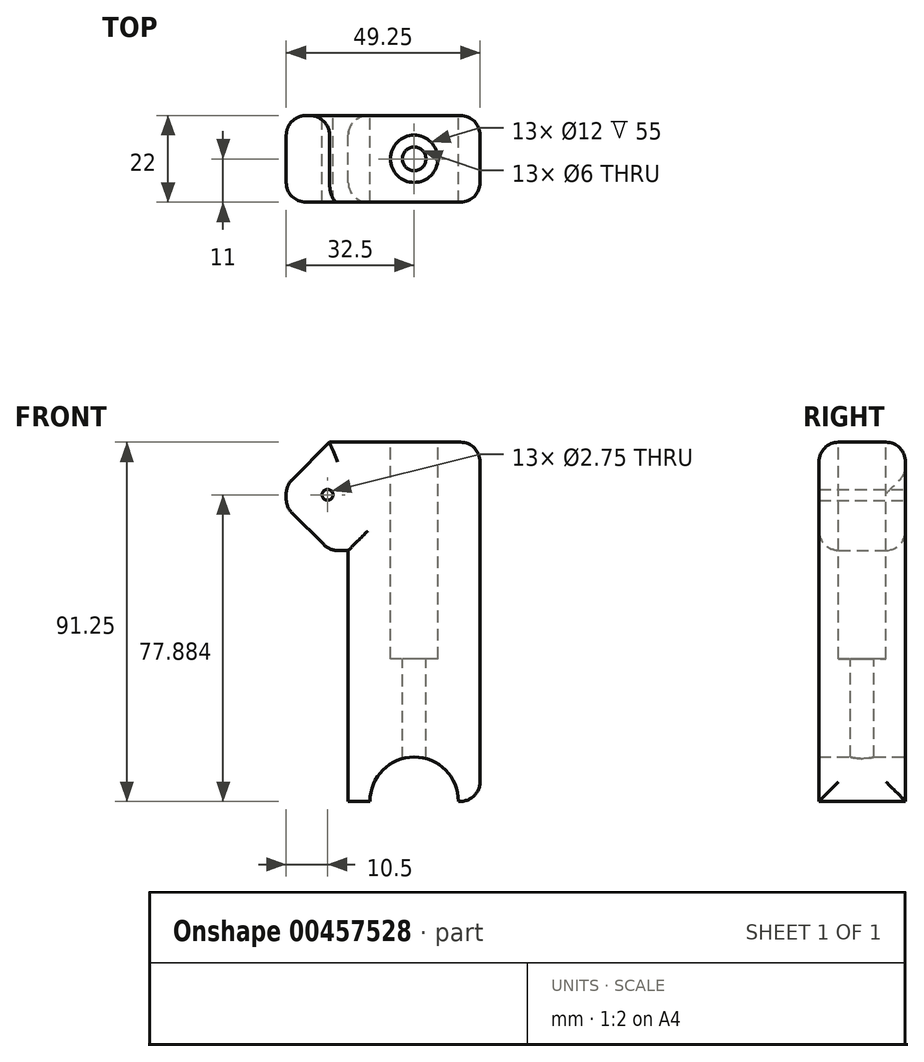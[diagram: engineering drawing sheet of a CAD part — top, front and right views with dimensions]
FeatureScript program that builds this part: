
annotation { "Feature Type Name" : "Feature", "Feature Type Description" : "" }
export const myFeature = defineFeature(function(context is Context, id is Id, definition is map)
    precondition{}
    {
        {
            var Q0;
            Q0=qCreatedBy(makeId("Front.planeOp"),FACE);
            var sketch = newSketch(context, id + "F0", { "sketchPlane" : qUnion([Q0])});
            skCircle(sketch, "E0", {"center": v(0, 0) * mm, "radius": 11.25 * mm});
            skCircle(sketch, "E1", {"center": v(0, 0) * mm, "radius": 16.75 * mm});
            skLineSegment(sketch, "E2", {"start": v(0, 11.25) * mm, "end": v(0, 36.25) * mm, "construction": true});
            skLineSegment(sketch, "E3.bottom", {"start": v(27.5, 36.25) * mm, "end": v(-27.5, 36.25) * mm});
            skLineSegment(sketch, "E3.top", {"start": v(27.5, -36.25) * mm, "end": v(-27.5, -36.25) * mm});
            skLineSegment(sketch, "E3.left", {"start": v(27.5, 36.25) * mm, "end": v(27.5, -36.25) * mm});
            skLineSegment(sketch, "E3.right", {"start": v(-27.5, 36.25) * mm, "end": v(-27.5, -36.25) * mm});
            skLineSegment(sketch, "E4", {"start": v(0, 36.25) * mm, "end": v(0, 91.25) * mm, "construction": true});
            skLineSegment(sketch, "E5.top", {"start": v(27.5, 91.25) * mm, "end": v(-27.5, 91.25) * mm});
            skLineSegment(sketch, "E5.left", {"start": v(27.5, 36.25) * mm, "end": v(27.5, 91.25) * mm});
            skLineSegment(sketch, "E5.right", {"start": v(-27.5, 36.25) * mm, "end": v(-27.5, 91.25) * mm});
            skPoint(sketch, "E5.middle", {"position": v(0, 63.75) * mm});
            skLineSegment(sketch, "E6", {"start": v(-27.5, 0) * mm, "end": v(27.5, 0) * mm});
            skLineSegment(sketch, "E7.bottom", {"start": v(-16.75, 63.75) * mm, "end": v(16.75, 63.75) * mm});
            skLineSegment(sketch, "E7.top", {"start": v(-16.75, -63.75) * mm, "end": v(16.75, -63.75) * mm});
            skLineSegment(sketch, "E7.left", {"start": v(-16.75, 63.75) * mm, "end": v(-16.75, -63.75) * mm});
            skLineSegment(sketch, "E7.right", {"start": v(16.75, 63.75) * mm, "end": v(16.75, -63.75) * mm});
            skLineSegment(sketch, "E8", {"start": v(-16.75, 63.75) * mm, "end": v(-27.5, 63.75) * mm});
            skLineSegment(sketch, "E9", {"start": v(16.75, 63.75) * mm, "end": v(27.5, 63.75) * mm});
            skLineSegment(sketch, "E10", {"start": v(16.75, 63.75) * mm, "end": v(16.75, 91.25) * mm});
            skLineSegment(sketch, "E11", {"start": v(0, 77.88) * mm, "end": v(-22, 77.88) * mm, "construction": true});
            skCircle(sketch, "E12", {"center": v(-22, 77.88) * mm, "radius": 1.38 * mm});
            skLineSegment(sketch, "E13", {"start": v(-27.5, 91.25) * mm, "end": v(-32.5, 91.25) * mm});
            skLineSegment(sketch, "E14", {"start": v(-32.5, 91.25) * mm, "end": v(-32.5, 63.78) * mm});
            skLineSegment(sketch, "E15", {"start": v(-32.5, 63.78) * mm, "end": v(-27.5, 63.75) * mm});
            skLineSegment(sketch, "E16", {"start": v(0, 70.14) * mm, "end": v(-5.5, 70.14) * mm, "construction": true});
            skLineSegment(sketch, "E17", {"start": v(-5.5, 63.75) * mm, "end": v(-5.5, 91.25) * mm});
            skSolve(sketch);
        }
        {
            var Q0;
            {var subQ5=sQuery(id+"F0.wireOp",EDGE,"E7.bottom");Q0=makeQuery(id+"F0.imprint","IMPRINT",FACE,{"disambiguationData":[TD([[makeQuery(id+"F0.imprint","IMPRINT",EDGE,{"derivedFrom":subQ5}),-1.0]])]});}
            var Q1;
            {var subQ4=sQuery(id+"F0.wireOp",EDGE,"E7.right");var subQ6=sQuery(id+"F0.wireOp",EDGE,"E3.bottom");var subQ7=makeQuery(id+"F0.imprint","INTERSECT",VERTEX,{"derivedFrom":[subQ6,subQ4]});Q1=makeQuery(id+"F0.imprint","IMPRINT",FACE,{"disambiguationData":[TD([[makeQuery(id+"F0.imprint","IMPRINT",EDGE,{"disambiguationData":[TD([[subQ7,-1.0]])],"derivedFrom":subQ6}),1.0]])]});}
            var Q2;
            {var subQ0=sQuery(id+"F0.wireOp",EDGE,"E6");var subQ1=sQuery(id+"F0.wireOp",EDGE,"E0");var subQ2=makeQuery(id+"F0.imprint","INTERSECT",VERTEX,{"disambiguationData":[OD(0.0)],"derivedFrom":[subQ1,subQ0]});Q2=makeQuery(id+"F0.imprint","IMPRINT",FACE,{"disambiguationData":[TD([[makeQuery(id+"F0.imprint","IMPRINT",EDGE,{"disambiguationData":[TD([[subQ2,1.0]])],"derivedFrom":subQ1}),-1.0]])]});}
            var Q3;
            Q3=makeQuery(id+"F0.imprint","IMPRINT",FACE,{"disambiguationData":[TD([[makeQuery(id+"F0.imprint","IMPRINT",EDGE,{"derivedFrom":sQuery(id+"F0.wireOp",EDGE,"E7.bottom")}),1.0]])]});
            var Q4;
            {var subQ0=sQuery(id+"F0.wireOp",EDGE,"E13");Q4=makeQuery(id+"F0.imprint","IMPRINT",FACE,{"disambiguationData":[TD([[makeQuery(id+"F0.imprint","IMPRINT",EDGE,{"derivedFrom":subQ0}),1.0]])]});}
            var Q5;
            {var subQ3=sQuery(id+"F0.wireOp",EDGE,"E8");Q5=makeQuery(id+"F0.imprint","IMPRINT",FACE,{"disambiguationData":[TD([[makeQuery(id+"F0.imprint","IMPRINT",EDGE,{"derivedFrom":subQ3}),-1.0]])]});}
            extrude(context, id + "F1", {"entities" : qUnion([Q0, Q1, Q2, Q3, Q4, Q5]), "endBound" : BoundingType.SYMMETRIC, "depth" : 22 * mm});
        }
        {
            var Q0;
            Q0=makeQuery(id+"F1.opExtrude","SWEPT_FACE",FACE,{"disambiguationData":[OSD([sQuery(id+"F0.wireOp",EDGE,"E5.top")])]});
            cPlane(context, id + "F2", {"entities" : qUnion([Q0]), "cplaneType" : CPlaneType.OFFSET, "offset" : 0 * mm, "width" : 150 * mm, "height" : 150 * mm});
        }
        {
            var Q0;
            Q0=qCreatedBy(id+"F2.planeOp",FACE);
            var sketch = newSketch(context, id + "F3", { "sketchPlane" : qUnion([Q0])});
            skCircle(sketch, "E18", {"center": v(0, 0) * mm, "radius": 6 * mm});
            skCircle(sketch, "E19", {"center": v(0, 0) * mm, "radius": 3 * mm});
            skSolve(sketch);
        }
        {
            var Q0;
            Q0=makeQuery(id+"F3.imprint","IMPRINT",FACE,{"disambiguationData":[TD([[makeQuery(id+"F3.imprint","IMPRINT",EDGE,{"derivedFrom":sQuery(id+"F3.wireOp",EDGE,"E18")}),1.0]])]});
            extrude(context, id + "F4", {"entities" : qUnion([Q0]), "operationType" : NewBodyOperationType.REMOVE, "oppositeDirection" : true, "depth" : 55 * mm});
        }
        {
            var Q0;
            Q0=makeQuery(id+"F3.imprint","IMPRINT",FACE,{"disambiguationData":[TD([[makeQuery(id+"F3.imprint","IMPRINT",EDGE,{"derivedFrom":sQuery(id+"F3.wireOp",EDGE,"E19")}),1.0]])]});
            extrude(context, id + "F5", {"entities" : qUnion([Q0]), "operationType" : NewBodyOperationType.REMOVE, "endBound" : BoundingType.THROUGH_ALL, "oppositeDirection" : true, "depth" : 25 * mm});
        }
        {
            var Q0;
            Q0=makeQuery(id+"F1.opExtrude","SWEPT_EDGE",EDGE,{"disambiguationData":[OSD([sQuery(id+"F0.wireOp",EDGE,"E14"),sQuery(id+"F0.wireOp",EDGE,"E15")])]});
            var Q1;
            Q1=makeQuery(id+"F1.opExtrude","SWEPT_EDGE",EDGE,{"disambiguationData":[OSD([sQuery(id+"F0.wireOp",EDGE,"E13"),sQuery(id+"F0.wireOp",EDGE,"E14")])]});
            chamfer(context, id + "F6", {"entities" : qUnion([Q0, Q1]), "width" : 11 * mm, "tangentPropagation" : true});
        }
        {
            var Q0;
            Q0=makeQuery(id+"F1.opExtrude","SWEPT_FACE",FACE,{"disambiguationData":[OSD([sQuery(id+"F0.wireOp",EDGE,"E7.right"),sQuery(id+"F0.wireOp",EDGE,"E10")])]});
            var Q1;
            Q1=makeQuery(id+"F1.opExtrude","CAP_EDGE",EDGE,{"disambiguationData":[OSD([sQuery(id+"F0.wireOp",EDGE,"E7.left")])],"isStart":false});
            var Q2;
            Q2=makeQuery(id+"F1.opExtrude","CAP_EDGE",EDGE,{"disambiguationData":[OSD([sQuery(id+"F0.wireOp",EDGE,"E7.left")])],"isStart":true});
            var Q3;
            {var subQ0=sQuery(id+"F0.wireOp",EDGE,"E5.right");Q3=makeQuery(id+"F6.opChamfer","BLEND_EDGE",EDGE,{"blendedFrom":[makeQuery(id+"F1.opExtrude","SWEPT_EDGE",EDGE,{"disambiguationData":[OSD([subQ0,sQuery(id+"F0.wireOp",EDGE,"E8")])]}),makeQuery(id+"F1.opExtrude","SWEPT_FACE",FACE,{"disambiguationData":[OSD([subQ0])]})],"blendedInto":[makeQuery(id+"F1.opExtrude","SWEPT_FACE",FACE,{"disambiguationData":[OSD([subQ0])]})]});}
            var Q4;
            {var subQ0=sQuery(id+"F0.wireOp",EDGE,"E5.right");Q4=makeQuery(id+"F6.opChamfer","BLEND_EDGE",EDGE,{"blendedFrom":[makeQuery(id+"F1.opExtrude","SWEPT_EDGE",EDGE,{"disambiguationData":[OSD([sQuery(id+"F0.wireOp",EDGE,"E5.top"),subQ0])]}),makeQuery(id+"F1.opExtrude","SWEPT_FACE",FACE,{"disambiguationData":[OSD([subQ0])]})],"blendedInto":[makeQuery(id+"F1.opExtrude","SWEPT_FACE",FACE,{"disambiguationData":[OSD([subQ0])]})]});}
            var Q5;
            {var subQ2=sQuery(id+"F0.wireOp",EDGE,"E5.right");var subQ7=sQuery(id+"F0.wireOp",EDGE,"E5.top");Q5=makeQuery(id+"F6.opChamfer","BLEND_EDGE",EDGE,{"blendedFrom":[makeQuery(id+"F1.opExtrude","SWEPT_EDGE",EDGE,{"disambiguationData":[OSD([subQ7,subQ2])]}),makeQuery(id+"F4.boolean.opBoolean","SPLIT",FACE,{"disambiguationData":[TD([makeQuery(id+"F1.opExtrude","SWEPT_FACE",FACE,{"disambiguationData":[OSD([subQ2])]})])],"derivedFrom":makeQuery(id+"F1.opExtrude","SWEPT_FACE",FACE,{"disambiguationData":[OSD([subQ7])]})})],"blendedInto":[makeQuery(id+"F4.boolean.opBoolean","SPLIT",FACE,{"disambiguationData":[TD([makeQuery(id+"F1.opExtrude","SWEPT_FACE",FACE,{"disambiguationData":[OSD([subQ2])]})])],"derivedFrom":makeQuery(id+"F1.opExtrude","SWEPT_FACE",FACE,{"disambiguationData":[OSD([subQ7])]})})]});}
            var Q6;
            Q6=makeQuery(id+"F1.opExtrude","CAP_EDGE",EDGE,{"disambiguationData":[OSD([sQuery(id+"F0.wireOp",EDGE,"E5.top")])],"isStart":false});
            var Q7;
            {var subQ0=sQuery(id+"F0.wireOp",EDGE,"E5.right");var subQ1=sQuery(id+"F0.wireOp",EDGE,"E5.top");Q7=makeQuery(id+"F6.opChamfer","BLEND_EDGE",EDGE,{"blendedFrom":[makeQuery(id+"F1.opExtrude","SWEPT_EDGE",EDGE,{"disambiguationData":[OSD([subQ1,subQ0])]}),makeQuery(id+"F1.opExtrude","CAP_FACE",FACE,{"disambiguationData":[OSD([sQuery(id+"F0.wireOp",EDGE,"E0"),subQ1,subQ0,sQuery(id+"F0.wireOp",EDGE,"E6"),sQuery(id+"F0.wireOp",EDGE,"E7.left"),sQuery(id+"F0.wireOp",EDGE,"E7.right"),sQuery(id+"F0.wireOp",EDGE,"E8"),sQuery(id+"F0.wireOp",EDGE,"E10"),sQuery(id+"F0.wireOp",EDGE,"E12")])],"isStart":false})],"blendedInto":[makeQuery(id+"F1.opExtrude","CAP_FACE",FACE,{"disambiguationData":[OSD([sQuery(id+"F0.wireOp",EDGE,"E0"),subQ1,subQ0,sQuery(id+"F0.wireOp",EDGE,"E6"),sQuery(id+"F0.wireOp",EDGE,"E7.left"),sQuery(id+"F0.wireOp",EDGE,"E7.right"),sQuery(id+"F0.wireOp",EDGE,"E8"),sQuery(id+"F0.wireOp",EDGE,"E10"),sQuery(id+"F0.wireOp",EDGE,"E12")])],"isStart":false})]});}
            var Q8;
            {var subQ0=sQuery(id+"F0.wireOp",EDGE,"E8");var subQ1=sQuery(id+"F0.wireOp",EDGE,"E5.right");Q8=makeQuery(id+"F6.opChamfer","BLEND_EDGE",EDGE,{"blendedFrom":[makeQuery(id+"F1.opExtrude","SWEPT_EDGE",EDGE,{"disambiguationData":[OSD([subQ1,subQ0])]}),makeQuery(id+"F1.opExtrude","CAP_FACE",FACE,{"disambiguationData":[OSD([sQuery(id+"F0.wireOp",EDGE,"E0"),sQuery(id+"F0.wireOp",EDGE,"E5.top"),subQ1,sQuery(id+"F0.wireOp",EDGE,"E6"),sQuery(id+"F0.wireOp",EDGE,"E7.left"),sQuery(id+"F0.wireOp",EDGE,"E7.right"),subQ0,sQuery(id+"F0.wireOp",EDGE,"E10"),sQuery(id+"F0.wireOp",EDGE,"E12")])],"isStart":false})],"blendedInto":[makeQuery(id+"F1.opExtrude","CAP_FACE",FACE,{"disambiguationData":[OSD([sQuery(id+"F0.wireOp",EDGE,"E0"),sQuery(id+"F0.wireOp",EDGE,"E5.top"),subQ1,sQuery(id+"F0.wireOp",EDGE,"E6"),sQuery(id+"F0.wireOp",EDGE,"E7.left"),sQuery(id+"F0.wireOp",EDGE,"E7.right"),subQ0,sQuery(id+"F0.wireOp",EDGE,"E10"),sQuery(id+"F0.wireOp",EDGE,"E12")])],"isStart":false})]});}
            var Q9;
            {var subQ0=sQuery(id+"F0.wireOp",EDGE,"E8");var subQ1=sQuery(id+"F0.wireOp",EDGE,"E5.right");Q9=makeQuery(id+"F6.opChamfer","BLEND_EDGE",EDGE,{"blendedFrom":[makeQuery(id+"F1.opExtrude","SWEPT_EDGE",EDGE,{"disambiguationData":[OSD([subQ1,subQ0])]}),makeQuery(id+"F1.opExtrude","CAP_FACE",FACE,{"disambiguationData":[OSD([sQuery(id+"F0.wireOp",EDGE,"E0"),sQuery(id+"F0.wireOp",EDGE,"E5.top"),subQ1,sQuery(id+"F0.wireOp",EDGE,"E6"),sQuery(id+"F0.wireOp",EDGE,"E7.left"),sQuery(id+"F0.wireOp",EDGE,"E7.right"),subQ0,sQuery(id+"F0.wireOp",EDGE,"E10"),sQuery(id+"F0.wireOp",EDGE,"E12")])],"isStart":true})],"blendedInto":[makeQuery(id+"F1.opExtrude","CAP_FACE",FACE,{"disambiguationData":[OSD([sQuery(id+"F0.wireOp",EDGE,"E0"),sQuery(id+"F0.wireOp",EDGE,"E5.top"),subQ1,sQuery(id+"F0.wireOp",EDGE,"E6"),sQuery(id+"F0.wireOp",EDGE,"E7.left"),sQuery(id+"F0.wireOp",EDGE,"E7.right"),subQ0,sQuery(id+"F0.wireOp",EDGE,"E10"),sQuery(id+"F0.wireOp",EDGE,"E12")])],"isStart":true})]});}
            var Q10;
            {var subQ0=sQuery(id+"F0.wireOp",EDGE,"E5.right");var subQ1=sQuery(id+"F0.wireOp",EDGE,"E5.top");Q10=makeQuery(id+"F6.opChamfer","BLEND_EDGE",EDGE,{"blendedFrom":[makeQuery(id+"F1.opExtrude","SWEPT_EDGE",EDGE,{"disambiguationData":[OSD([subQ1,subQ0])]}),makeQuery(id+"F1.opExtrude","CAP_FACE",FACE,{"disambiguationData":[OSD([sQuery(id+"F0.wireOp",EDGE,"E0"),subQ1,subQ0,sQuery(id+"F0.wireOp",EDGE,"E6"),sQuery(id+"F0.wireOp",EDGE,"E7.left"),sQuery(id+"F0.wireOp",EDGE,"E7.right"),sQuery(id+"F0.wireOp",EDGE,"E8"),sQuery(id+"F0.wireOp",EDGE,"E10"),sQuery(id+"F0.wireOp",EDGE,"E12")])],"isStart":true})],"blendedInto":[makeQuery(id+"F1.opExtrude","CAP_FACE",FACE,{"disambiguationData":[OSD([sQuery(id+"F0.wireOp",EDGE,"E0"),subQ1,subQ0,sQuery(id+"F0.wireOp",EDGE,"E6"),sQuery(id+"F0.wireOp",EDGE,"E7.left"),sQuery(id+"F0.wireOp",EDGE,"E7.right"),sQuery(id+"F0.wireOp",EDGE,"E8"),sQuery(id+"F0.wireOp",EDGE,"E10"),sQuery(id+"F0.wireOp",EDGE,"E12")])],"isStart":true})]});}
            var Q11;
            Q11=makeQuery(id+"F1.opExtrude","CAP_EDGE",EDGE,{"disambiguationData":[OSD([sQuery(id+"F0.wireOp",EDGE,"E5.top")])],"isStart":true});
            var Q12;
            {var subQ0=sQuery(id+"F0.wireOp",EDGE,"E14");Q12=makeQuery(id+"F6.opChamfer","BLEND_EDGE",EDGE,{"blendedFrom":[makeQuery(id+"F1.opExtrude","SWEPT_EDGE",EDGE,{"disambiguationData":[OSD([sQuery(id+"F0.wireOp",EDGE,"E13"),subQ0])]}),makeQuery(id+"F1.opExtrude","SWEPT_FACE",FACE,{"disambiguationData":[OSD([subQ0])]})],"blendedInto":[makeQuery(id+"F1.opExtrude","SWEPT_FACE",FACE,{"disambiguationData":[OSD([subQ0])]})]});}
            var Q13;
            {var subQ0=sQuery(id+"F0.wireOp",EDGE,"E14");Q13=makeQuery(id+"F6.opChamfer","BLEND_EDGE",EDGE,{"blendedFrom":[makeQuery(id+"F1.opExtrude","SWEPT_EDGE",EDGE,{"disambiguationData":[OSD([subQ0,sQuery(id+"F0.wireOp",EDGE,"E15")])]}),makeQuery(id+"F1.opExtrude","SWEPT_FACE",FACE,{"disambiguationData":[OSD([subQ0])]})],"blendedInto":[makeQuery(id+"F1.opExtrude","SWEPT_FACE",FACE,{"disambiguationData":[OSD([subQ0])]})]});}
            var Q14;
            Q14=makeQuery(id+"F6.opChamfer","BLEND_EDGE",EDGE,{"blendedFrom":[makeQuery(id+"F1.opExtrude","SWEPT_EDGE",EDGE,{"disambiguationData":[OSD([sQuery(id+"F0.wireOp",EDGE,"E14"),sQuery(id+"F0.wireOp",EDGE,"E15")])]}),makeQuery(id+"F1.opExtrude","SWEPT_FACE",FACE,{"disambiguationData":[OSD([sQuery(id+"F0.wireOp",EDGE,"E8")])]})],"blendedInto":[makeQuery(id+"F1.opExtrude","SWEPT_FACE",FACE,{"disambiguationData":[OSD([sQuery(id+"F0.wireOp",EDGE,"E8")])]})]});
            var Q15;
            Q15=makeQuery(id+"F1.opExtrude","CAP_EDGE",EDGE,{"disambiguationData":[OSD([sQuery(id+"F0.wireOp",EDGE,"E8")])],"isStart":false});
            var Q16;
            {var subQ0=sQuery(id+"F0.wireOp",EDGE,"E15");var subQ1=sQuery(id+"F0.wireOp",EDGE,"E14");Q16=makeQuery(id+"F6.opChamfer","BLEND_EDGE",EDGE,{"blendedFrom":[makeQuery(id+"F1.opExtrude","SWEPT_EDGE",EDGE,{"disambiguationData":[OSD([subQ1,subQ0])]}),makeQuery(id+"F1.opExtrude","CAP_FACE",FACE,{"disambiguationData":[OSD([sQuery(id+"F0.wireOp",EDGE,"E0"),sQuery(id+"F0.wireOp",EDGE,"E5.top"),sQuery(id+"F0.wireOp",EDGE,"E6"),sQuery(id+"F0.wireOp",EDGE,"E7.left"),sQuery(id+"F0.wireOp",EDGE,"E7.right"),sQuery(id+"F0.wireOp",EDGE,"E8"),sQuery(id+"F0.wireOp",EDGE,"E10"),sQuery(id+"F0.wireOp",EDGE,"E12"),sQuery(id+"F0.wireOp",EDGE,"E13"),subQ1,subQ0])],"isStart":false})],"blendedInto":[makeQuery(id+"F1.opExtrude","CAP_FACE",FACE,{"disambiguationData":[OSD([sQuery(id+"F0.wireOp",EDGE,"E0"),sQuery(id+"F0.wireOp",EDGE,"E5.top"),sQuery(id+"F0.wireOp",EDGE,"E6"),sQuery(id+"F0.wireOp",EDGE,"E7.left"),sQuery(id+"F0.wireOp",EDGE,"E7.right"),sQuery(id+"F0.wireOp",EDGE,"E8"),sQuery(id+"F0.wireOp",EDGE,"E10"),sQuery(id+"F0.wireOp",EDGE,"E12"),sQuery(id+"F0.wireOp",EDGE,"E13"),subQ1,subQ0])],"isStart":false})]});}
            var Q17;
            Q17=makeQuery(id+"F1.opExtrude","CAP_EDGE",EDGE,{"disambiguationData":[OSD([sQuery(id+"F0.wireOp",EDGE,"E14")])],"isStart":false});
            var Q18;
            Q18=makeQuery(id+"F1.opExtrude","CAP_EDGE",EDGE,{"disambiguationData":[OSD([sQuery(id+"F0.wireOp",EDGE,"E14")])],"isStart":true});
            var Q19;
            Q19=makeQuery(id+"F1.opExtrude","CAP_EDGE",EDGE,{"disambiguationData":[OSD([sQuery(id+"F0.wireOp",EDGE,"E8")])],"isStart":true});
            var Q20;
            {var subQ0=sQuery(id+"F0.wireOp",EDGE,"E15");var subQ1=sQuery(id+"F0.wireOp",EDGE,"E14");Q20=makeQuery(id+"F6.opChamfer","BLEND_EDGE",EDGE,{"blendedFrom":[makeQuery(id+"F1.opExtrude","SWEPT_EDGE",EDGE,{"disambiguationData":[OSD([subQ1,subQ0])]}),makeQuery(id+"F1.opExtrude","CAP_FACE",FACE,{"disambiguationData":[OSD([sQuery(id+"F0.wireOp",EDGE,"E0"),sQuery(id+"F0.wireOp",EDGE,"E5.top"),sQuery(id+"F0.wireOp",EDGE,"E6"),sQuery(id+"F0.wireOp",EDGE,"E7.left"),sQuery(id+"F0.wireOp",EDGE,"E7.right"),sQuery(id+"F0.wireOp",EDGE,"E8"),sQuery(id+"F0.wireOp",EDGE,"E10"),sQuery(id+"F0.wireOp",EDGE,"E12"),sQuery(id+"F0.wireOp",EDGE,"E13"),subQ1,subQ0])],"isStart":true})],"blendedInto":[makeQuery(id+"F1.opExtrude","CAP_FACE",FACE,{"disambiguationData":[OSD([sQuery(id+"F0.wireOp",EDGE,"E0"),sQuery(id+"F0.wireOp",EDGE,"E5.top"),sQuery(id+"F0.wireOp",EDGE,"E6"),sQuery(id+"F0.wireOp",EDGE,"E7.left"),sQuery(id+"F0.wireOp",EDGE,"E7.right"),sQuery(id+"F0.wireOp",EDGE,"E8"),sQuery(id+"F0.wireOp",EDGE,"E10"),sQuery(id+"F0.wireOp",EDGE,"E12"),sQuery(id+"F0.wireOp",EDGE,"E13"),subQ1,subQ0])],"isStart":true})]});}
            var Q21;
            Q21=makeQuery(id+"F1.opExtrude","SWEPT_EDGE",EDGE,{"disambiguationData":[OSD([sQuery(id+"F0.wireOp",EDGE,"E1"),sQuery(id+"F0.wireOp",EDGE,"E6"),sQuery(id+"F0.wireOp",EDGE,"E7.right")])]});
            var Q22;
            {var subQ0=sQuery(id+"F0.wireOp",EDGE,"E14");var subQ1=sQuery(id+"F0.wireOp",EDGE,"E13");Q22=makeQuery(id+"F6.opChamfer","BLEND_EDGE",EDGE,{"blendedFrom":[makeQuery(id+"F1.opExtrude","SWEPT_EDGE",EDGE,{"disambiguationData":[OSD([subQ1,subQ0])]}),makeQuery(id+"F1.opExtrude","CAP_FACE",FACE,{"disambiguationData":[OSD([sQuery(id+"F0.wireOp",EDGE,"E0"),sQuery(id+"F0.wireOp",EDGE,"E5.top"),sQuery(id+"F0.wireOp",EDGE,"E6"),sQuery(id+"F0.wireOp",EDGE,"E7.left"),sQuery(id+"F0.wireOp",EDGE,"E7.right"),sQuery(id+"F0.wireOp",EDGE,"E8"),sQuery(id+"F0.wireOp",EDGE,"E10"),sQuery(id+"F0.wireOp",EDGE,"E12"),subQ1,subQ0,sQuery(id+"F0.wireOp",EDGE,"E15")])],"isStart":false})],"blendedInto":[makeQuery(id+"F1.opExtrude","CAP_FACE",FACE,{"disambiguationData":[OSD([sQuery(id+"F0.wireOp",EDGE,"E0"),sQuery(id+"F0.wireOp",EDGE,"E5.top"),sQuery(id+"F0.wireOp",EDGE,"E6"),sQuery(id+"F0.wireOp",EDGE,"E7.left"),sQuery(id+"F0.wireOp",EDGE,"E7.right"),sQuery(id+"F0.wireOp",EDGE,"E8"),sQuery(id+"F0.wireOp",EDGE,"E10"),sQuery(id+"F0.wireOp",EDGE,"E12"),subQ1,subQ0,sQuery(id+"F0.wireOp",EDGE,"E15")])],"isStart":false})]});}
            fillet(context, id + "F7", {"entities" : qUnion([Q0, Q1, Q2, Q3, Q4, Q5, Q6, Q7, Q8, Q9, Q10, Q11, Q12, Q13, Q14, Q15, Q16, Q17, Q18, Q19, Q20, Q21, Q22]), "radius" : 5 * mm, "tangentPropagation" : true, "allowEdgeOverflow" : false});
        }
    });
